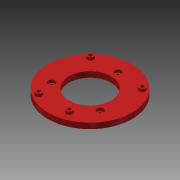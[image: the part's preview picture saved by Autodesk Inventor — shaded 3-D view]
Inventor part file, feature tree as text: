
AUTODESK INVENTOR PART (.ipt)
format: ipt  version: 2014 (Build 180170000, 170)  size: 138,752 bytes
history: native  units: in
note: dims shown in document units (in); Inventor stores cm internally (conversion verified against a paired STEP export)
features: sketch x4, extrude x3, hole x1, pattern_circular x1
ambient origin geometry x8: Origin, YZ Plane, XZ Plane, XY Plane, X Axis, Y Axis, Z Axis, Center Point
bodies: Solid1 (feature_tree)
feature tree (9):
  extrude  "Extrusion1"  Depth=0.25in
  hole  "Hole1"  [1 undecoded]
  pattern_circular  "Circular Pattern1"  Count=3 Angle=360.0deg
  extrude  "Extrusion2"  Depth=0.12in
  extrude  "Extrusion3"  Depth=0.1in
  sketch  "Sketch1"  dims[d0=2.0in d1=0.25in]
  sketch  "Sketch2"  dims[d3=0.2in d4=0.0in d5=3.0in]
  sketch  "Sketch4"  dims[d6=1.0in]
  sketch  "Sketch5"  dims[d7=0.12in d8=0.75in d9=0.24in d10=0.1in d11=0.5635in d12=1.0in d13=0.8108in d14=1.1811in d15=360.0deg d17=0.12in d18=1.1in d19=0.6in d20=0.2in d21=2.0in d22=0.05in d23=1.3225in d24=1.3225in d25=1.3225in d26=1.0in d27=0.0in d28=0.225in d29=0.1in d30=0.0in]
note: 1 required parameter value undecoded (feature->parameter linkage not recoverable at this tier; creation-order binding heuristic only, values carry confidence <= 0.55)
